# Revit family: 3-407-xxx - Pivot
name_source: partatom
category: Luminarias
units: mm (PartAtom-declared; Revit-internal decimal feet)

## family parameters
Anfitrión = Techo
Compartido = No
Corte con vacíos al cargar = No
Cota de conector redondo = Diámetro de uso
Número OmniClass = 23.80.70.11
Origen de luz = Sí
Punto de cálculo de habitación = No
Siempre vertical = Sí
Tipo de pieza = Normal
Título OmniClass = Luminaries for Internal Lighting

## types (3) — shared parameters
Cambio de temperatura de color de luz atenuada = <Ninguno>
Diffusers = White Frost Glass
Diámetro de círculo de emisión = 610 mm
Fabricante = Oxygen - Lighting & Fans
Filtro de color = 16777215
Forma visible en renderización = No
Metal Finish 1 = 40 - Aged Brass
Modelo = 3-407-xx Pivot Pendant
References = Ref. 3 = 120 V / Ref. 37 = 277 V
Tamaño de símbolo de origen de luz = 610 mm
URL = www.oxygenlighting.com
Voltage = 120 V
Voltage Input = 120 V or 277 V - 50/60 Hz
zero-valued in all types: Elevación por defecto

## per-type parameters (varying)
| type | Metal Finish 2 |
| 3-407-1540 / Black - Aged Brass | 15 - Black |
| 3-407-640 / White - Aged Brass | 06 - White |
| 3-407-40 / Aged Brass | 40 - Aged Brass |

## geometry (parser evidence)
native form markers: Sweep x5
no freeform markers — native parametric forms only
